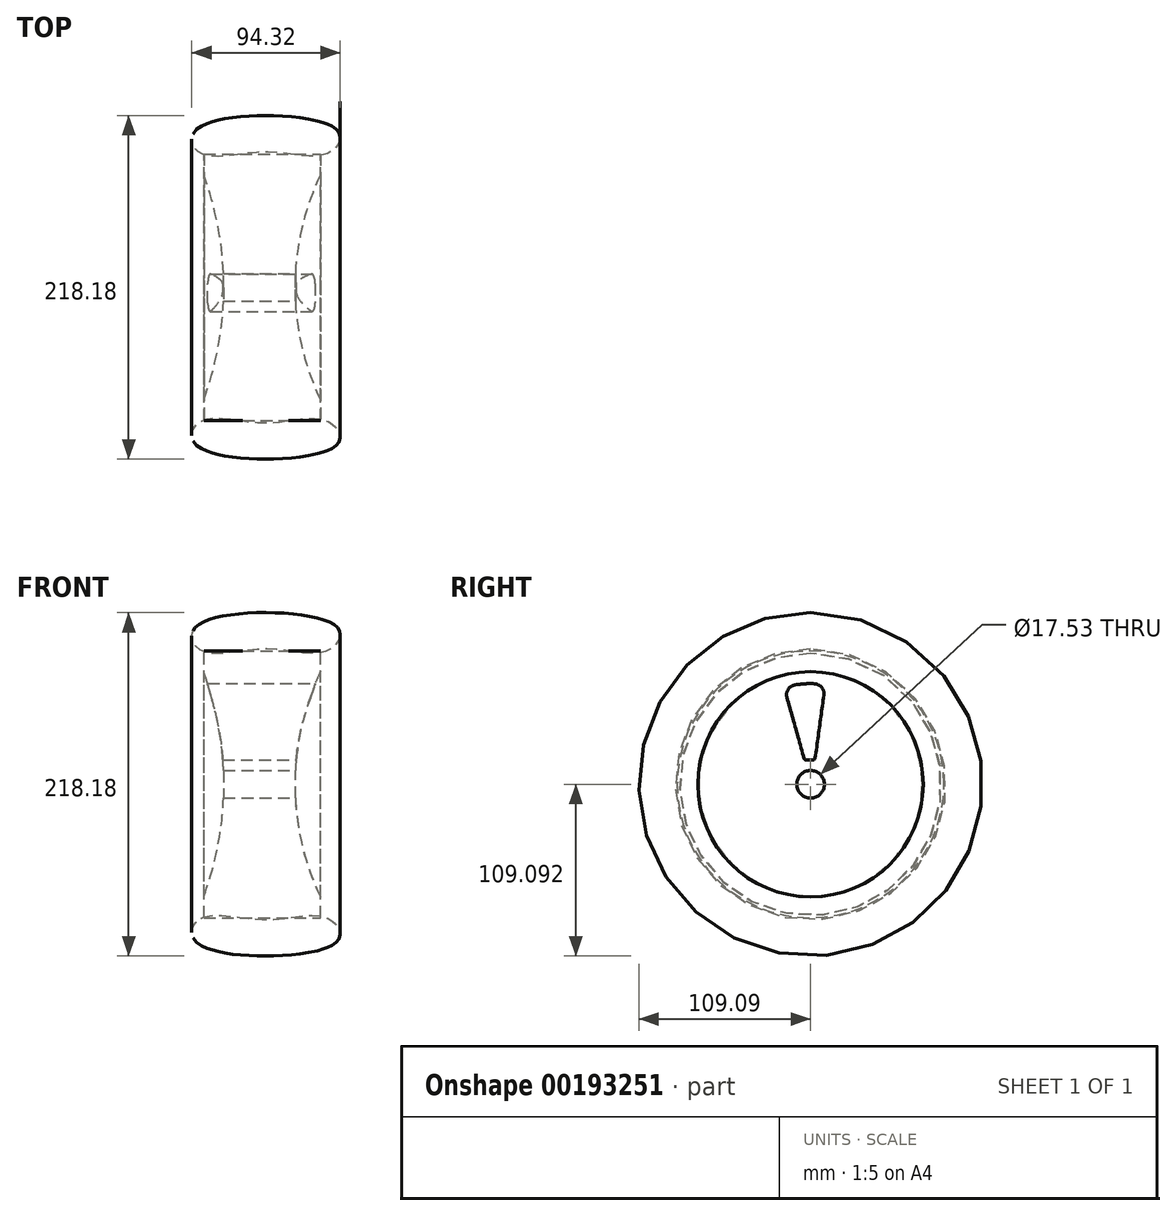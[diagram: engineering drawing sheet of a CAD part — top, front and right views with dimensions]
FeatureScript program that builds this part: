
annotation { "Feature Type Name" : "Feature", "Feature Type Description" : "" }
export const myFeature = defineFeature(function(context is Context, id is Id, definition is map)
    precondition{}
    {
        {
            var Q0;
            Q0=qCreatedBy(makeId("Front.planeOp"),FACE);
            var sketch = newSketch(context, id + "F0", { "sketchPlane" : qUnion([Q0])});
            skFitSpline(sketch, "E0", {"points": [v(-45.95, 59.69) * mm, v(0, 71.3) * mm, v(47.21, 59.69) * mm, v(38.57, 46.82) * mm, v(0, 48.17) * mm, v(-40.05, 46.82) * mm, v(-45.95, 59.69) * mm]});
            skLineSegment(sketch, "E1", {"start": v(60.57, -37.79) * mm, "end": v(-60.53, -37.79) * mm, "construction": true});
            skSolve(sketch);
        }
        {
            var Q0;
            Q0=makeQuery(id+"F0.imprint","IMPRINT",FACE,{"disambiguationData":[TD([[makeQuery(id+"F0.imprint","IMPRINT",EDGE,{"derivedFrom":sQuery(id+"F0.wireOp",EDGE,"E0")}),-1.0]])]});
            var Q1;
            Q1=sQuery(id+"F0.wireOp",EDGE,"E1");
            revolve(context, id + "F1", {"entities" : qUnion([Q0]), "axis" : qUnion([Q1]), "revolveType" : RevolveType.FULL});
        }
        {
            var Q0;
            Q0=qCreatedBy(makeId("Front.planeOp"),FACE);
            var sketch = newSketch(context, id + "F2", { "sketchPlane" : qUnion([Q0])});
            skLineSegment(sketch, "E2", {"start": v(-38.99, 46.95) * mm, "end": v(35.04, 46.95) * mm});
            skLineSegment(sketch, "E3", {"start": v(35.04, 46.95) * mm, "end": v(35.04, 33.74) * mm});
            skLineSegment(sketch, "E4", {"start": v(18.85, -37.79) * mm, "end": v(-26.36, -37.79) * mm});
            skArc(sketch, "E5", {"start": v(-26.36, -37.79) * mm, "mid": v(-29.54, -1.76) * mm, "end": v(-38.99, 33.14) * mm});
            skLineSegment(sketch, "E6.trimOffspring", {"start": v(-38.99, 33.14) * mm, "end": v(-38.99, 46.95) * mm});
            skArc(sketch, "E7", {"start": v(35.04, 33.74) * mm, "mid": v(22.95, -1.12) * mm, "end": v(18.85, -37.79) * mm});
            skLineSegment(sketch, "E8", {"start": v(18.85, -37.79) * mm, "end": v(18.85, -81.08) * mm, "construction": true});
            skLineSegment(sketch, "E9", {"start": v(-26.36, -37.79) * mm, "end": v(-26.36, -82.65) * mm, "construction": true});
            skSolve(sketch);
        }
        {
            var Q0;
            Q0 = qSketchRegion(id + "F2", true);
            var Q1;
            Q1=sQuery(id+"F0.wireOp",EDGE,"E1");
            revolve(context, id + "F3", {"entities" : qUnion([Q0]), "axis" : qUnion([Q1]), "revolveType" : RevolveType.FULL});
        }
        {
            var Q0;
            Q0=makeQuery(id+"F3.opRevolve","SWEPT_FACE",FACE,{"disambiguationData":[OSD([sQuery(id+"F2.wireOp",EDGE,"E3")])]});
            var sketch = newSketch(context, id + "F4", { "sketchPlane" : qUnion([Q0])});
            skCircle(sketch, "E10", {"center": v(0, -37.79) * mm, "radius": 15.6 * mm, "construction": true});
            skCircle(sketch, "E11", {"center": v(0, -37.79) * mm, "radius": 63.95 * mm, "construction": true});
            skLineSegment(sketch, "E12", {"start": v(-4.08, -21.5) * mm, "end": v(-15, 17.4) * mm});
            skLineSegment(sketch, "E13", {"start": v(8.46, 18.9) * mm, "end": v(2.94, -21.17) * mm});
            skArc(sketch, "E14", {"start": v(2.4, 26.11) * mm, "mid": v(-3.75, 26.05) * mm, "end": v(-9.87, 25.4) * mm});
            skArc(sketch, "E15", {"start": v(1.56, -22.26) * mm, "mid": v(-0.55, -22.19) * mm, "end": v(-2.64, -22.4) * mm});
            skPoint(sketch, "E16.visualSharp", {"position": v(-16.83, 23.9) * mm});
            skArc(sketch, "E16.filletArc", {"start": v(-9.87, 25.4) * mm, "mid": v(-14.23, 22.55) * mm, "end": v(-15, 17.4) * mm});
            skPoint(sketch, "E17.visualSharp", {"position": v(9.36, 25.47) * mm});
            skArc(sketch, "E17.filletArc", {"start": v(8.46, 18.9) * mm, "mid": v(7.03, 23.85) * mm, "end": v(2.4, 26.11) * mm});
            skPoint(sketch, "E18.visualSharp", {"position": v(-3.76, -22.64) * mm});
            skArc(sketch, "E18.filletArc", {"start": v(-4.08, -21.5) * mm, "mid": v(-3.54, -22.23) * mm, "end": v(-2.64, -22.4) * mm});
            skPoint(sketch, "E19.visualSharp", {"position": v(2.77, -22.43) * mm});
            skArc(sketch, "E19.filletArc", {"start": v(1.56, -22.26) * mm, "mid": v(2.47, -22) * mm, "end": v(2.94, -21.17) * mm});
            skSolve(sketch);
        }
        {
            var Q0;
            Q0 = qSketchRegion(id + "F4", true);
            extrude(context, id + "F5", {"entities" : qUnion([Q0]), "operationType" : NewBodyOperationType.REMOVE, "endBound" : BoundingType.THROUGH_ALL, "oppositeDirection" : true, "depth" : 25.4 * mm});
        }
        {
            var Q0;
            Q0=qCreatedBy(makeId("Right.planeOp"),FACE);
            var sketch = newSketch(context, id + "F6", { "sketchPlane" : qUnion([Q0])});
            skCircle(sketch, "E20", {"center": v(0, -37.79) * mm, "radius": 8.76 * mm});
            skSolve(sketch);
        }
        {
            var Q0;
            Q0 = qSketchRegion(id + "F6", true);
            extrude(context, id + "F7", {"entities" : qUnion([Q0]), "operationType" : NewBodyOperationType.REMOVE, "endBound" : BoundingType.THROUGH_ALL, "oppositeDirection" : true, "depth" : 25.4 * mm, "hasSecondDirection" : true, "secondDirectionBound" : SecondDirectionBoundingType.THROUGH_ALL, "secondDirectionOppositeDirection" : false, "secondDirectionDepth" : 25.4 * mm});
        }
    });
